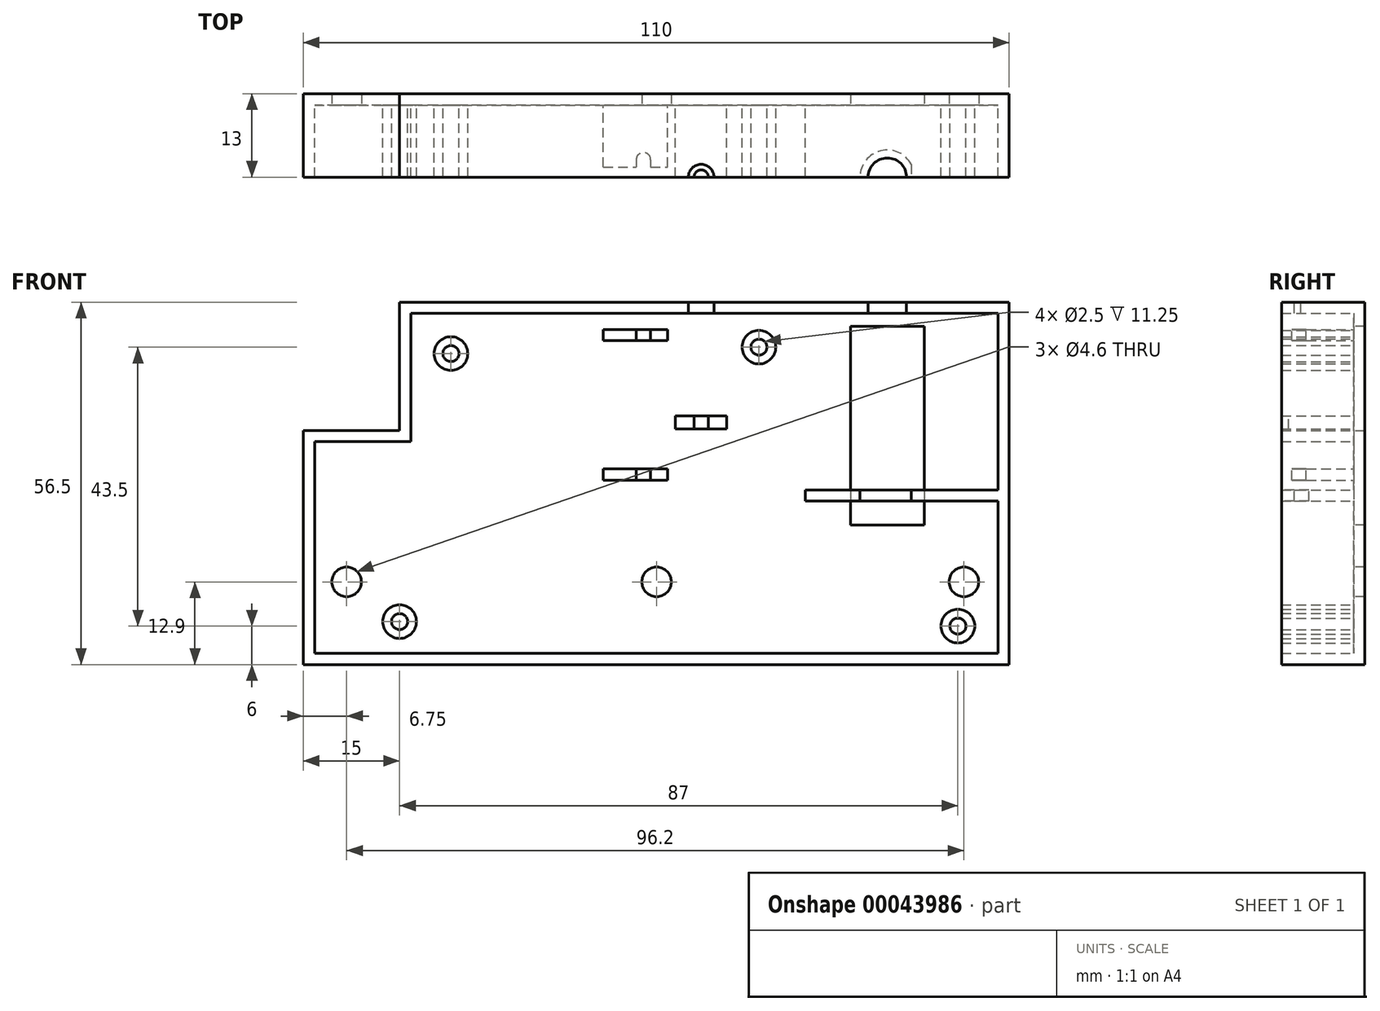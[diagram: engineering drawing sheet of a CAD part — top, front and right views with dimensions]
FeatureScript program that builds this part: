
annotation { "Feature Type Name" : "Feature", "Feature Type Description" : "" }
export const myFeature = defineFeature(function(context is Context, id is Id, definition is map)
    precondition{}
    {
        {
            var Q0;
            Q0=qCreatedBy(makeId("Front.planeOp"),FACE);
            var sketch = newSketch(context, id + "F0", { "sketchPlane" : qUnion([Q0])});
            skLineSegment(sketch, "E0", {"start": v(0, 0) * mm, "end": v(110, 0) * mm});
            skLineSegment(sketch, "E1", {"start": v(110, 0) * mm, "end": v(110, 56.5) * mm});
            skLineSegment(sketch, "E2", {"start": v(110, 56.5) * mm, "end": v(15, 56.5) * mm});
            skLineSegment(sketch, "E3", {"start": v(15, 56.5) * mm, "end": v(15, 36.5) * mm});
            skLineSegment(sketch, "E4", {"start": v(15, 36.5) * mm, "end": v(0, 36.5) * mm});
            skLineSegment(sketch, "E5", {"start": v(0, 36.5) * mm, "end": v(0, 0) * mm});
            skSolve(sketch);
        }
        {
            var Q0;
            Q0 = qSketchRegion(id + "F0", true);
            extrude(context, id + "F1", {"entities" : qUnion([Q0]), "depth" : 13 * mm});
        }
        {
            var Q0;
            Q0=makeQuery(id+"F1.opExtrude","CAP_FACE",FACE,{"disambiguationData":[OSD([sQuery(id+"F0.wireOp",EDGE,"E0"),sQuery(id+"F0.wireOp",EDGE,"E1"),sQuery(id+"F0.wireOp",EDGE,"E2"),sQuery(id+"F0.wireOp",EDGE,"E3"),sQuery(id+"F0.wireOp",EDGE,"E4"),sQuery(id+"F0.wireOp",EDGE,"E5")])],"isStart":false});
            shell(context, id + "F2", {"entities" : qUnion([Q0]), "thickness" : 1.75 * mm});
        }
        {
            var Q0;
            Q0=makeQuery(id+"F2.opShell","OFFSET_FACE",FACE,{"disambiguationData":[OSD([sQuery(id+"F0.wireOp",EDGE,"E0"),sQuery(id+"F0.wireOp",EDGE,"E1"),sQuery(id+"F0.wireOp",EDGE,"E2"),sQuery(id+"F0.wireOp",EDGE,"E3"),sQuery(id+"F0.wireOp",EDGE,"E4"),sQuery(id+"F0.wireOp",EDGE,"E5")])]});
            var sketch = newSketch(context, id + "F3", { "sketchPlane" : qUnion([Q0])});
            skCircle(sketch, "E6", {"center": v(23, 48.5) * mm, "radius": 2.62 * mm});
            skCircle(sketch, "E7", {"center": v(15, 6.7) * mm, "radius": 2.62 * mm});
            skCircle(sketch, "E8", {"center": v(71, 49.5) * mm, "radius": 2.63 * mm});
            skCircle(sketch, "E9", {"center": v(102, 6) * mm, "radius": 2.62 * mm});
            skLineSegment(sketch, "E10", {"start": v(108.25, 27.25) * mm, "end": v(78.25, 27.25) * mm});
            skLineSegment(sketch, "E11", {"start": v(78.25, 27.25) * mm, "end": v(78.25, 25.5) * mm});
            skLineSegment(sketch, "E12", {"start": v(78.25, 25.5) * mm, "end": v(108.25, 25.5) * mm});
            skLineSegment(sketch, "E13.bottom", {"start": v(58, 38.75) * mm, "end": v(66, 38.75) * mm});
            skLineSegment(sketch, "E13.top", {"start": v(58, 36.75) * mm, "end": v(66, 36.75) * mm});
            skLineSegment(sketch, "E13.left", {"start": v(58, 38.75) * mm, "end": v(58, 36.75) * mm});
            skLineSegment(sketch, "E13.right", {"start": v(66, 38.75) * mm, "end": v(66, 36.75) * mm});
            skLineSegment(sketch, "E14", {"start": v(108.25, 25.5) * mm, "end": v(108.25, 27.25) * mm});
            skCircle(sketch, "E15", {"center": v(23, 48.5) * mm, "radius": 1.25 * mm});
            skCircle(sketch, "E16", {"center": v(15, 6.7) * mm, "radius": 1.25 * mm});
            skCircle(sketch, "E17", {"center": v(71, 49.5) * mm, "radius": 1.25 * mm});
            skCircle(sketch, "E18", {"center": v(102, 6) * mm, "radius": 1.25 * mm});
            skSolve(sketch);
        }
        {
            var Q0;
            Q0 = qSketchRegion(id + "F3", true);
            var Q1;
            Q1=makeQuery(id+"F1.opExtrude","CAP_FACE",FACE,{"disambiguationData":[OSD([sQuery(id+"F0.wireOp",EDGE,"E0"),sQuery(id+"F0.wireOp",EDGE,"E1"),sQuery(id+"F0.wireOp",EDGE,"E2"),sQuery(id+"F0.wireOp",EDGE,"E3"),sQuery(id+"F0.wireOp",EDGE,"E4"),sQuery(id+"F0.wireOp",EDGE,"E5")])],"isStart":false});
            extrude(context, id + "F4", {"entities" : qUnion([Q0]), "operationType" : NewBodyOperationType.ADD, "endBound" : BoundingType.UP_TO_SURFACE, "endBoundEntityFace" : qUnion([Q1]), "depth" : 25 * mm});
        }
        {
            var Q0;
            Q0=makeQuery(id+"F1.opExtrude","SWEPT_FACE",FACE,{"disambiguationData":[OSD([sQuery(id+"F0.wireOp",EDGE,"E2")])]});
            var sketch = newSketch(context, id + "F5", { "sketchPlane" : qUnion([Q0])});
            skCircle(sketch, "E19", {"center": v(91, -13) * mm, "radius": 3 * mm});
            skCircle(sketch, "E20", {"center": v(62, -13) * mm, "radius": 2 * mm});
            skSolve(sketch);
        }
        {
            var Q0;
            Q0 = qSketchRegion(id + "F5", true);
            extrude(context, id + "F6", {"entities" : qUnion([Q0]), "operationType" : NewBodyOperationType.REMOVE, "oppositeDirection" : true, "depth" : 2 * mm});
        }
        {
            var Q0;
            Q0=makeQuery(id+"F4.opExtrude","SWEPT_FACE",FACE,{"disambiguationData":[OSD([sQuery(id+"F3.wireOp",EDGE,"E13.bottom")])]});
            var sketch = newSketch(context, id + "F7", { "sketchPlane" : qUnion([Q0])});
            skCircle(sketch, "E21", {"center": v(62, -13) * mm, "radius": 1.13 * mm});
            skSolve(sketch);
        }
        {
            var Q0;
            Q0 = qSketchRegion(id + "F7", true);
            extrude(context, id + "F8", {"entities" : qUnion([Q0]), "operationType" : NewBodyOperationType.REMOVE, "oppositeDirection" : true, "depth" : 2 * mm});
        }
        {
            var Q0;
            Q0=makeQuery(id+"F4.opExtrude","SWEPT_FACE",FACE,{"disambiguationData":[OSD([sQuery(id+"F3.wireOp",EDGE,"E10")])]});
            var sketch = newSketch(context, id + "F9", { "sketchPlane" : qUnion([Q0])});
            skArc(sketch, "E22", {"start": v(94.75, -11) * mm, "mid": v(86.75, -13) * mm, "end": v(94.75, -15) * mm});
            skLineSegment(sketch, "E23", {"start": v(94.75, -11) * mm, "end": v(94.75, -15) * mm});
            skSolve(sketch);
        }
        {
            var Q0;
            Q0 = qSketchRegion(id + "F9", true);
            extrude(context, id + "F10", {"entities" : qUnion([Q0]), "operationType" : NewBodyOperationType.REMOVE, "oppositeDirection" : true, "depth" : 2 * mm});
        }
        {
            var Q0;
            {var subQ0=sQuery(id+"F0.wireOp",EDGE,"E5");var subQ1=sQuery(id+"F0.wireOp",EDGE,"E4");var subQ2=sQuery(id+"F0.wireOp",EDGE,"E0");var subQ3=sQuery(id+"F0.wireOp",EDGE,"E1");var subQ4=sQuery(id+"F0.wireOp",EDGE,"E2");var subQ5=sQuery(id+"F0.wireOp",EDGE,"E3");Q0=makeQuery(id+"F4.boolean.opBoolean","SPLIT",FACE,{"disambiguationData":[TD([makeQuery(id+"F2.opShell","OFFSET_FACE",FACE,{"disambiguationData":[OSD([subQ2])]})])],"derivedFrom":makeQuery(id+"F2.opShell","OFFSET_FACE",FACE,{"disambiguationData":[OSD([subQ2,subQ3,subQ4,subQ5,subQ1,subQ0])]})});}
            var sketch = newSketch(context, id + "F11", { "sketchPlane" : qUnion([Q0])});
            skLineSegment(sketch, "E24.bottom", {"start": v(46.75, 52.25) * mm, "end": v(56.75, 52.25) * mm});
            skLineSegment(sketch, "E24.top", {"start": v(46.75, 50.5) * mm, "end": v(56.75, 50.5) * mm});
            skLineSegment(sketch, "E24.left", {"start": v(46.75, 52.25) * mm, "end": v(46.75, 50.5) * mm});
            skLineSegment(sketch, "E24.right", {"start": v(56.75, 52.25) * mm, "end": v(56.75, 50.5) * mm});
            skLineSegment(sketch, "E25.bottom", {"start": v(46.75, 30.5) * mm, "end": v(56.75, 30.5) * mm});
            skLineSegment(sketch, "E25.top", {"start": v(46.75, 28.75) * mm, "end": v(56.75, 28.75) * mm});
            skLineSegment(sketch, "E25.left", {"start": v(46.75, 30.5) * mm, "end": v(46.75, 28.75) * mm});
            skLineSegment(sketch, "E25.right", {"start": v(56.75, 30.5) * mm, "end": v(56.75, 28.75) * mm});
            skSolve(sketch);
        }
        {
            var Q0;
            Q0 = qSketchRegion(id + "F11", true);
            var Q1;
            {var subQ0=sQuery(id+"F0.wireOp",EDGE,"E0");var subQ1=makeQuery(id+"F2.opShell","OFFSET_FACE",FACE,{"disambiguationData":[OSD([subQ0])]});var subQ2=sQuery(id+"F0.wireOp",EDGE,"E3");var subQ3=makeQuery(id+"F2.opShell","OFFSET_FACE",FACE,{"disambiguationData":[OSD([subQ2])]});var subQ4=sQuery(id+"F0.wireOp",EDGE,"E5");var subQ5=makeQuery(id+"F1.opExtrude","SWEPT_FACE",FACE,{"disambiguationData":[OSD([subQ4])]});var subQ6=sQuery(id+"F0.wireOp",EDGE,"E4");var subQ7=makeQuery(id+"F1.opExtrude","SWEPT_FACE",FACE,{"disambiguationData":[OSD([subQ6])]});var subQ8=makeQuery(id+"F1.opExtrude","SWEPT_FACE",FACE,{"disambiguationData":[OSD([subQ0])]});var subQ9=sQuery(id+"F0.wireOp",EDGE,"E1");var subQ10=makeQuery(id+"F1.opExtrude","SWEPT_FACE",FACE,{"disambiguationData":[OSD([subQ9])]});var subQ11=sQuery(id+"F0.wireOp",EDGE,"E2");var subQ12=makeQuery(id+"F2.opShell","OFFSET_FACE",FACE,{"disambiguationData":[OSD([subQ11])]});var subQ13=makeQuery(id+"F1.opExtrude","SWEPT_FACE",FACE,{"disambiguationData":[OSD([subQ11])]});var subQ14=makeQuery(id+"F2.opShell","OFFSET_FACE",FACE,{"disambiguationData":[OSD([subQ4])]});var subQ15=makeQuery(id+"F2.opShell","OFFSET_FACE",FACE,{"disambiguationData":[OSD([subQ9])]});var subQ16=makeQuery(id+"F1.opExtrude","SWEPT_FACE",FACE,{"disambiguationData":[OSD([subQ2])]});var subQ17=sQuery(id+"F3.wireOp",EDGE,"E12");var subQ18=makeQuery(id+"F4.opExtrude","SWEPT_FACE",FACE,{"disambiguationData":[OSD([subQ17])]});var subQ19=makeQuery(id+"F2.opShell","OFFSET_FACE",FACE,{"disambiguationData":[OSD([subQ6])]});var subQ20=sQuery(id+"F3.wireOp",EDGE,"E10");var subQ21=makeQuery(id+"F4.opExtrude","SWEPT_FACE",FACE,{"disambiguationData":[OSD([subQ20])]});var subQ22=makeQuery(id+"F6.opExtrude","SWEPT_FACE",FACE,{"disambiguationData":[OSD([sQuery(id+"F5.wireOp",EDGE,"E19")])]});var subQ23=makeQuery(id+"F6.opExtrude","SWEPT_FACE",FACE,{"disambiguationData":[OSD([sQuery(id+"F5.wireOp",EDGE,"E20")])]});var subQ24=sQuery(id+"F3.wireOp",EDGE,"E11");Q1=makeQuery(id+"F10.boolean.opBoolean","SPLIT",FACE,{"disambiguationData":[TD([subQ8])],"derivedFrom":makeQuery(id+"F6.boolean.opBoolean","SPLIT",FACE,{"disambiguationData":[TD([subQ8,subQ10,subQ13,subQ16,subQ7,subQ5,subQ1,subQ15,subQ12,subQ3,subQ19,subQ14,subQ21,makeQuery(id+"F4.opExtrude","SWEPT_FACE",FACE,{"disambiguationData":[OSD([subQ24])]}),subQ18,subQ22,subQ23])],"derivedFrom":makeQuery(id+"F4.boolean.opBoolean","MERGE",FACE,{"derivedFrom":[makeQuery(id+"F1.opExtrude","CAP_FACE",FACE,{"disambiguationData":[OSD([subQ0,subQ9,subQ11,subQ2,subQ6,subQ4])],"isStart":false}),makeQuery(id+"F4.opExtrude","CAP_FACE",FACE,{"disambiguationData":[OSD([subQ0,subQ9,subQ11,subQ2,subQ6,subQ4]),ownerDisambiguation([makeQuery(id+"F4.opExtrude","SWEPT_BODY",BODY,{"disambiguationData":[OSD([subQ20,subQ24,subQ17,sQuery(id+"F3.wireOp",EDGE,"E14")])]})])],"isStart":false})]})})});}
            extrude(context, id + "F12", {"entities" : qUnion([Q0]), "operationType" : NewBodyOperationType.ADD, "endBound" : BoundingType.UP_TO_SURFACE, "endBoundEntityFace" : qUnion([Q1]), "depth" : 25 * mm});
        }
        {
            var Q0;
            Q0=makeQuery(id+"F12.opExtrude","CAP_FACE",FACE,{"disambiguationData":[OSD([sQuery(id+"F11.wireOp",EDGE,"E24.bottom"),sQuery(id+"F11.wireOp",EDGE,"E24.top"),sQuery(id+"F11.wireOp",EDGE,"E24.left"),sQuery(id+"F11.wireOp",EDGE,"E24.right")])],"isStart":false});
            var sketch = newSketch(context, id + "F13", { "sketchPlane" : qUnion([Q0])});
            skLineSegment(sketch, "E26.0.0", {"start": v(56.75, 52.25) * mm, "end": v(46.75, 52.25) * mm});
            skLineSegment(sketch, "E26.0.1", {"start": v(46.75, 52.25) * mm, "end": v(46.75, 50.5) * mm});
            skLineSegment(sketch, "E26.0.2", {"start": v(46.75, 50.5) * mm, "end": v(56.75, 50.5) * mm});
            skLineSegment(sketch, "E26.0.3", {"start": v(56.75, 50.5) * mm, "end": v(56.75, 52.25) * mm});
            skLineSegment(sketch, "E27.0.0", {"start": v(56.75, 30.5) * mm, "end": v(46.75, 30.5) * mm});
            skLineSegment(sketch, "E27.0.1", {"start": v(46.75, 30.5) * mm, "end": v(46.75, 28.75) * mm});
            skLineSegment(sketch, "E27.0.2", {"start": v(46.75, 28.75) * mm, "end": v(56.75, 28.75) * mm});
            skLineSegment(sketch, "E27.0.3", {"start": v(56.75, 28.75) * mm, "end": v(56.75, 30.5) * mm});
            skSolve(sketch);
        }
        {
            var Q0;
            Q0 = qSketchRegion(id + "F13", true);
            extrude(context, id + "F14", {"entities" : qUnion([Q0]), "operationType" : NewBodyOperationType.REMOVE, "oppositeDirection" : true, "depth" : 1.6 * mm});
        }
        {
            var Q0;
            Q0=makeQuery(id+"F12.opExtrude","SWEPT_FACE",FACE,{"disambiguationData":[OSD([sQuery(id+"F11.wireOp",EDGE,"E24.bottom")])]});
            var sketch = newSketch(context, id + "F15", { "sketchPlane" : qUnion([Q0])});
            skArc(sketch, "E28", {"start": v(54.12, -10.3) * mm, "mid": v(53, -9.15) * mm, "end": v(51.88, -10.3) * mm});
            skLineSegment(sketch, "E29", {"start": v(51.88, -10.3) * mm, "end": v(51.9, -11.4) * mm});
            skLineSegment(sketch, "E30", {"start": v(54.12, -10.3) * mm, "end": v(54.1, -11.4) * mm});
            skLineSegment(sketch, "E31", {"start": v(51.9, -11.4) * mm, "end": v(54.1, -11.4) * mm});
            skSolve(sketch);
        }
        {
            var Q0;
            Q0 = qSketchRegion(id + "F15", true);
            extrude(context, id + "F16", {"entities" : qUnion([Q0]), "operationType" : NewBodyOperationType.REMOVE, "oppositeDirection" : true, "depth" : 25 * mm});
        }
        {
            var Q0;
            {var subQ0=sQuery(id+"F0.wireOp",EDGE,"E5");var subQ1=sQuery(id+"F0.wireOp",EDGE,"E4");var subQ2=sQuery(id+"F0.wireOp",EDGE,"E0");var subQ3=sQuery(id+"F0.wireOp",EDGE,"E1");var subQ4=sQuery(id+"F0.wireOp",EDGE,"E2");var subQ5=sQuery(id+"F0.wireOp",EDGE,"E3");Q0=makeQuery(id+"F4.boolean.opBoolean","SPLIT",FACE,{"disambiguationData":[TD([makeQuery(id+"F2.opShell","OFFSET_FACE",FACE,{"disambiguationData":[OSD([subQ2])]})])],"derivedFrom":makeQuery(id+"F2.opShell","OFFSET_FACE",FACE,{"disambiguationData":[OSD([subQ2,subQ3,subQ4,subQ5,subQ1,subQ0])]})});}
            var sketch = newSketch(context, id + "F17", { "sketchPlane" : qUnion([Q0])});
            skLineSegment(sketch, "E32.bottom", {"start": v(85.25, 52.75) * mm, "end": v(96.75, 52.75) * mm});
            skLineSegment(sketch, "E32.top", {"start": v(85.25, 21.75) * mm, "end": v(96.75, 21.75) * mm});
            skLineSegment(sketch, "E32.left", {"start": v(85.25, 52.75) * mm, "end": v(85.25, 21.75) * mm});
            skLineSegment(sketch, "E32.right", {"start": v(96.75, 52.75) * mm, "end": v(96.75, 21.75) * mm});
            skSolve(sketch);
        }
        {
            var Q0;
            Q0 = qSketchRegion(id + "F17", true);
            extrude(context, id + "F18", {"entities" : qUnion([Q0]), "operationType" : NewBodyOperationType.REMOVE, "endBound" : BoundingType.THROUGH_ALL, "oppositeDirection" : true, "depth" : 25 * mm});
        }
        {
            var Q0;
            {var subQ0=sQuery(id+"F0.wireOp",EDGE,"E5");var subQ1=sQuery(id+"F0.wireOp",EDGE,"E4");var subQ2=sQuery(id+"F0.wireOp",EDGE,"E0");var subQ3=sQuery(id+"F0.wireOp",EDGE,"E1");var subQ4=sQuery(id+"F0.wireOp",EDGE,"E2");var subQ5=sQuery(id+"F0.wireOp",EDGE,"E3");Q0=makeQuery(id+"F4.boolean.opBoolean","SPLIT",FACE,{"disambiguationData":[TD([makeQuery(id+"F2.opShell","OFFSET_FACE",FACE,{"disambiguationData":[OSD([subQ2])]})])],"derivedFrom":makeQuery(id+"F2.opShell","OFFSET_FACE",FACE,{"disambiguationData":[OSD([subQ2,subQ3,subQ4,subQ5,subQ1,subQ0])]})});}
            var sketch = newSketch(context, id + "F19", { "sketchPlane" : qUnion([Q0])});
            skCircle(sketch, "E33", {"center": v(6.75, 12.9) * mm, "radius": 2.3 * mm});
            skCircle(sketch, "E34", {"center": v(55.05, 12.9) * mm, "radius": 2.3 * mm});
            skCircle(sketch, "E35", {"center": v(102.95, 12.9) * mm, "radius": 2.3 * mm});
            skSolve(sketch);
        }
        {
            var Q0;
            Q0 = qSketchRegion(id + "F19", true);
            extrude(context, id + "F20", {"entities" : qUnion([Q0]), "operationType" : NewBodyOperationType.REMOVE, "endBound" : BoundingType.THROUGH_ALL, "oppositeDirection" : true, "depth" : 25 * mm});
        }
    });
